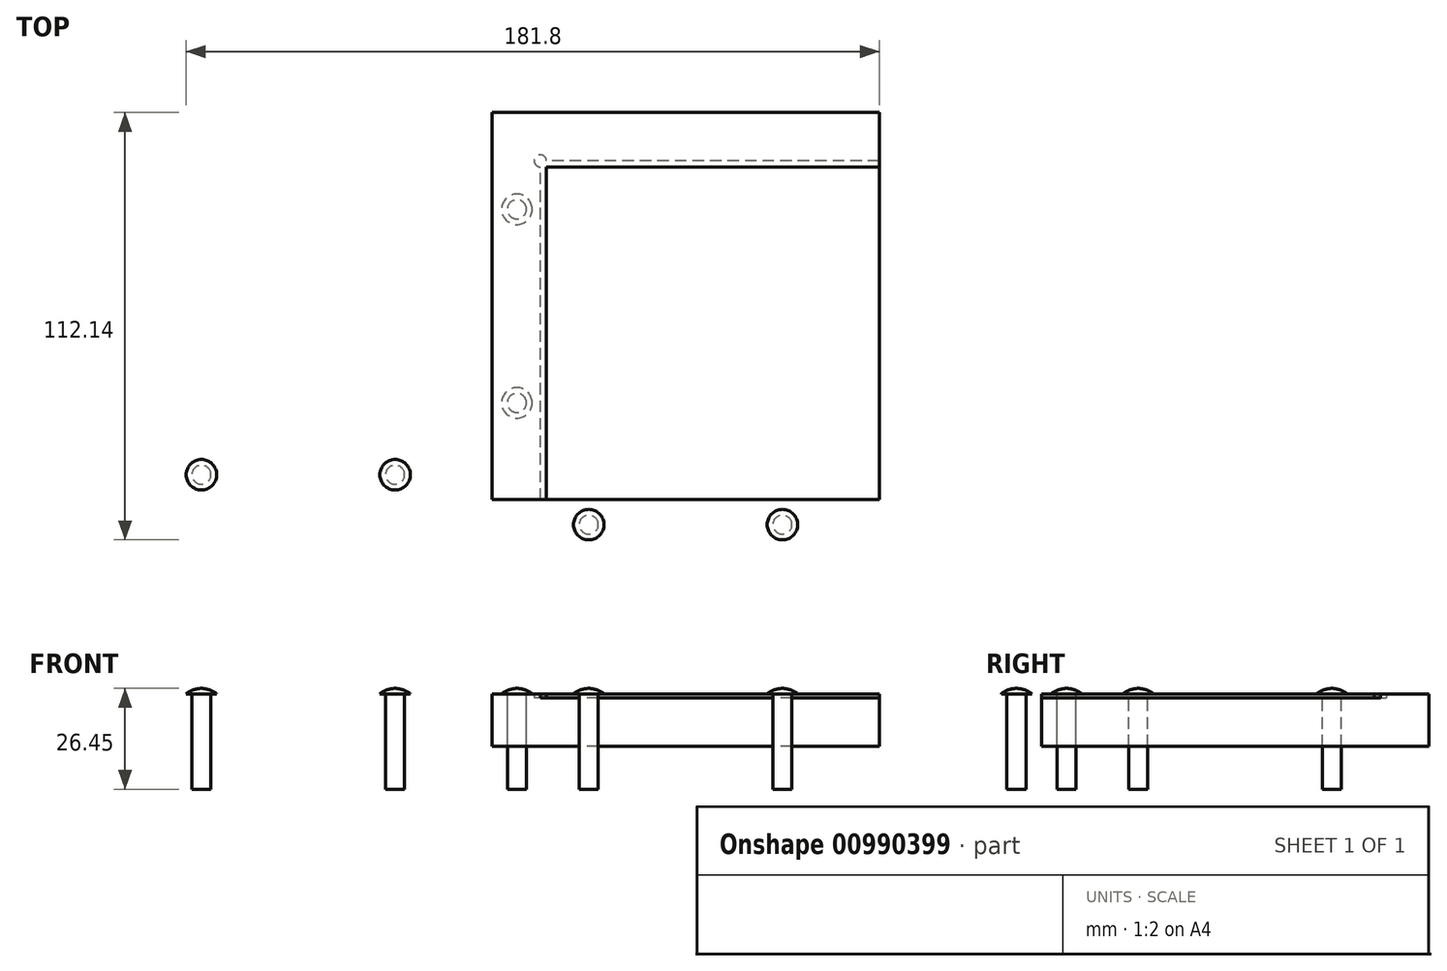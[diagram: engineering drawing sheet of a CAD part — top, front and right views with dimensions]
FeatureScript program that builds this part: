
annotation { "Feature Type Name" : "Feature", "Feature Type Description" : "" }
export const myFeature = defineFeature(function(context is Context, id is Id, definition is map)
    precondition{}
    {
        {
            var Q0;
            Q0=qCreatedBy(makeId("Top.planeOp"),FACE);
            var sketch = newSketch(context, id + "F0", { "sketchPlane" : qUnion([Q0])});
            skLineSegment(sketch, "E0.bottom", {"start": v(50.8, 50.8) * mm, "end": v(-50.8, 50.8) * mm});
            skLineSegment(sketch, "E0.top", {"start": v(50.8, -50.8) * mm, "end": v(-50.8, -50.8) * mm});
            skLineSegment(sketch, "E0.left", {"start": v(50.8, 50.8) * mm, "end": v(50.8, -50.8) * mm});
            skLineSegment(sketch, "E0.right", {"start": v(-50.8, 50.8) * mm, "end": v(-50.8, -50.8) * mm});
            skPoint(sketch, "E0.middle", {"position": v(0, 0) * mm});
            skSolve(sketch);
        }
        {
            var Q0;
            Q0=makeQuery(id+"F0.imprint","IMPRINT",FACE,{"disambiguationData":[TD([[makeQuery(id+"F0.imprint","IMPRINT",EDGE,{"derivedFrom":sQuery(id+"F0.wireOp",EDGE,"E0.bottom")}),1.0]])]});
            extrude(context, id + "F1", {"entities" : qUnion([Q0]), "depth" : 12.7 * mm, "offsetDistance" : 25.4 * mm});
        }
        {
            var Q0;
            Q0=makeQuery(id+"F1.opExtrude","CAP_FACE",FACE,{"disambiguationData":[OSD([sQuery(id+"F0.wireOp",EDGE,"E0.bottom"),sQuery(id+"F0.wireOp",EDGE,"E0.top"),sQuery(id+"F0.wireOp",EDGE,"E0.left"),sQuery(id+"F0.wireOp",EDGE,"E0.right")])],"isStart":false});
            var sketch = newSketch(context, id + "F2", { "sketchPlane" : qUnion([Q0])});
            skLineSegment(sketch, "E1.bottom", {"start": v(50.8, -50.8) * mm, "end": v(-38.1, -50.8) * mm});
            skLineSegment(sketch, "E1.top", {"start": v(50.8, 38.1) * mm, "end": v(-36.51, 38.1) * mm});
            skLineSegment(sketch, "E1.left", {"start": v(50.8, -50.8) * mm, "end": v(50.8, 38.1) * mm});
            skLineSegment(sketch, "E1.right", {"start": v(-38.1, -50.8) * mm, "end": v(-38.1, 36.51) * mm});
            skArc(sketch, "E2", {"start": v(-36.51, 38.1) * mm, "mid": v(-39.22, 39.22) * mm, "end": v(-38.1, 36.51) * mm});
            skLineSegment(sketch, "E3.bottom", {"start": v(-38.1, -50.8) * mm, "end": v(-36.51, -50.8) * mm});
            skLineSegment(sketch, "E3.top", {"start": v(-36.51, 38.1) * mm, "end": v(-36.51, 38.1) * mm});
            skLineSegment(sketch, "E3.right", {"start": v(-36.51, -50.8) * mm, "end": v(-36.51, 36.51) * mm});
            skLineSegment(sketch, "E4.top", {"start": v(50.8, 36.51) * mm, "end": v(-36.51, 36.51) * mm});
            skLineSegment(sketch, "E4.left", {"start": v(50.8, 38.1) * mm, "end": v(50.8, 36.51) * mm});
            skSolve(sketch);
        }
        {
            var Q0;
            Q0=makeQuery(id+"F2.imprint","IMPRINT",FACE,{"disambiguationData":[TD([[makeQuery(id+"F2.imprint","IMPRINT",EDGE,{"derivedFrom":sQuery(id+"F2.wireOp",EDGE,"E2")}),-1.0]])]});
            extrude(context, id + "F3", {"entities" : qUnion([Q0]), "operationType" : NewBodyOperationType.ADD, "depth" : 1 * mm, "offsetDistance" : 25.4 * mm});
        }
        {
            var Q0;
            Q0=makeQuery(id+"F3.opExtrude","CAP_FACE",FACE,{"disambiguationData":[OSD([sQuery(id+"F0.wireOp",EDGE,"E0.bottom"),sQuery(id+"F0.wireOp",EDGE,"E0.top"),sQuery(id+"F0.wireOp",EDGE,"E0.left"),sQuery(id+"F0.wireOp",EDGE,"E0.right"),sQuery(id+"F2.wireOp",EDGE,"E2"),sQuery(id+"F2.wireOp",EDGE,"E3.top"),sQuery(id+"F2.wireOp",EDGE,"E1.right"),sQuery(id+"F2.wireOp",EDGE,"E1.top")])],"isStart":false});
            var sketch = newSketch(context, id + "F4", { "sketchPlane" : qUnion([Q0])});
            skLineSegment(sketch, "E5.0", {"start": v(50.8, 50.8) * mm, "end": v(-50.8, 50.8) * mm});
            skLineSegment(sketch, "E5.1", {"start": v(50.8, -50.8) * mm, "end": v(-50.8, -50.8) * mm});
            skLineSegment(sketch, "E5.2", {"start": v(50.8, 50.8) * mm, "end": v(50.8, -50.8) * mm});
            skLineSegment(sketch, "E5.3", {"start": v(-50.8, 50.8) * mm, "end": v(-50.8, -50.8) * mm});
            skPoint(sketch, "E5.4", {"position": v(0, 0) * mm});
            skLineSegment(sketch, "E5.5", {"start": v(50.8, -50.8) * mm, "end": v(-38.1, -50.8) * mm});
            skLineSegment(sketch, "E5.6", {"start": v(50.8, 38.1) * mm, "end": v(-36.51, 38.1) * mm});
            skLineSegment(sketch, "E5.7", {"start": v(50.8, -50.8) * mm, "end": v(50.8, 38.1) * mm});
            skLineSegment(sketch, "E5.8", {"start": v(-38.1, -50.8) * mm, "end": v(-38.1, 36.51) * mm});
            skArc(sketch, "E5.9", {"start": v(-36.51, 38.1) * mm, "mid": v(-39.22, 39.22) * mm, "end": v(-38.1, 36.51) * mm});
            skLineSegment(sketch, "E5.10", {"start": v(-38.1, -50.8) * mm, "end": v(-36.51, -50.8) * mm});
            skLineSegment(sketch, "E5.11", {"start": v(-36.51, 38.1) * mm, "end": v(-34.93, 38.1) * mm});
            skLineSegment(sketch, "E5.12", {"start": v(-38.1, -50.8) * mm, "end": v(-38.1, 36.51) * mm});
            skLineSegment(sketch, "E5.13", {"start": v(-36.51, -50.8) * mm, "end": v(-36.51, 36.51) * mm});
            skLineSegment(sketch, "E5.14", {"start": v(50.8, 38.1) * mm, "end": v(-36.51, 38.1) * mm});
            skLineSegment(sketch, "E5.15", {"start": v(50.8, 36.51) * mm, "end": v(-36.51, 36.51) * mm});
            skLineSegment(sketch, "E5.16", {"start": v(50.8, 38.1) * mm, "end": v(50.8, 36.51) * mm});
            skPoint(sketch, "E6", {"position": v(-44.26, 25.4) * mm});
            skSolve(sketch);
        }
        {
            var Q0;
            Q0=makeQuery(id+"F4.imprint","IMPRINT",FACE,{"disambiguationData":[TD([[makeQuery(id+"F4.imprint","IMPRINT",EDGE,{"derivedFrom":sQuery(id+"F4.wireOp",EDGE,"E5.0")}),1.0]])]});
            var Q1;
            Q1=makeQuery(id+"F4.imprint","IMPRINT",FACE,{"disambiguationData":[TD([[makeQuery(id+"F4.imprint","IMPRINT",EDGE,{"derivedFrom":sQuery(id+"F4.wireOp",EDGE,"E5.9")}),1.0]])]});
            extrude(context, id + "F5", {"entities" : qUnion([Q0, Q1]), "depth" : 1 / 203.2 * mm, "offsetDistance" : 25.4 * mm});
        }
        {
            var Q0;
            Q0=sQuery(id+"F4.wireOp",VERTEX,"E6");
            var Q1;
            Q1=qCreatedBy(makeId("Front.planeOp"),FACE);
            cPlane(context, id + "F6", {"entities" : qUnion([Q0, Q1]), "cplaneType" : CPlaneType.PLANE_POINT, "offset" : 25.4 * mm, "width" : 152.4 * mm, "height" : 152.4 * mm});
        }
        {
            var Q0;
            Q0=qCreatedBy(id+"F6.planeOp",FACE);
            var sketch = newSketch(context, id + "F7", { "sketchPlane" : qUnion([Q0])});
            skLineSegment(sketch, "E7", {"start": v(-46.76, 13.7) * mm, "end": v(-46.76, -11.3) * mm});
            skLineSegment(sketch, "E8", {"start": v(-46.76, -11.3) * mm, "end": v(-44.26, -11.3) * mm});
            skLineSegment(sketch, "E9", {"start": v(-44.26, -11.3) * mm, "end": v(-44.26, 15.15) * mm});
            skLineSegment(sketch, "E10", {"start": v(-46.76, 13.7) * mm, "end": v(-48.26, 13.7) * mm});
            skArc(sketch, "E11", {"start": v(-44.26, 15.15) * mm, "mid": v(-46.38, 14.78) * mm, "end": v(-48.26, 13.7) * mm});
            skPoint(sketch, "E12.orphan", {"position": v(-40.26, 13.7) * mm});
            skPoint(sketch, "E13", {"position": v(-44.26, 13.7) * mm});
            skLineSegment(sketch, "E14.bottom", {"start": v(-44.26, 13.7) * mm, "end": v(-46.5, 13.7) * mm});
            skLineSegment(sketch, "E14.top", {"start": v(-44.26, -11.3) * mm, "end": v(-46.5, -11.3) * mm});
            skLineSegment(sketch, "E14.left", {"start": v(-44.26, 13.7) * mm, "end": v(-44.26, -11.3) * mm});
            skLineSegment(sketch, "E14.right", {"start": v(-46.5, 13.7) * mm, "end": v(-46.5, -11.3) * mm});
            skSolve(sketch);
        }
        {
            var Q0;
            Q0=makeQuery(id+"F7.imprint","IMPRINT",FACE,{"disambiguationData":[TD([[makeQuery(id+"F7.imprint","IMPRINT",EDGE,{"derivedFrom":sQuery(id+"F7.wireOp",EDGE,"E7")}),1.0]])]});
            var Q1;
            Q1=makeQuery(id+"F7.imprint","IMPRINT",FACE,{"disambiguationData":[TD([[makeQuery(id+"F7.imprint","IMPRINT",EDGE,{"derivedFrom":sQuery(id+"F7.wireOp",EDGE,"E14.bottom")}),1.0]])]});
            var Q2;
            Q2=sQuery(id+"F7.wireOp",EDGE,"E14.left");
            revolve(context, id + "F8", {"surfaceOperationType" : NewSurfaceOperationType.NEW, "entities" : qUnion([Q0, Q1]), "axis" : qUnion([Q2]), "revolveType" : RevolveType.FULL});
        }
        {
            var Q0;
            Q0=makeQuery(id+"F8.opRevolve","SWEPT_BODY",BODY,{"disambiguationData":[OSD([sQuery(id+"F7.wireOp",EDGE,"E7"),sQuery(id+"F7.wireOp",EDGE,"E8"),sQuery(id+"F7.wireOp",EDGE,"E9"),sQuery(id+"F7.wireOp",EDGE,"E10"),sQuery(id+"F7.wireOp",EDGE,"E11"),sQuery(id+"F7.wireOp",EDGE,"E14.top"),sQuery(id+"F7.wireOp",EDGE,"E14.left")])]});
            var Q1;
            Q1=qCreatedBy(makeId("Front.planeOp"),FACE);
            mirror(context, id + "F9", {"entities" : qUnion([Q0]), "mirrorPlane" : qUnion([Q1])});
        }
        {
            var Q0;
            Q0=makeQuery(id+"F8.opRevolve","SWEPT_BODY",BODY,{"disambiguationData":[OSD([sQuery(id+"F7.wireOp",EDGE,"E7"),sQuery(id+"F7.wireOp",EDGE,"E8"),sQuery(id+"F7.wireOp",EDGE,"E9"),sQuery(id+"F7.wireOp",EDGE,"E10"),sQuery(id+"F7.wireOp",EDGE,"E11"),sQuery(id+"F7.wireOp",EDGE,"E14.top"),sQuery(id+"F7.wireOp",EDGE,"E14.left")])]});
            var Q1;
            Q1=makeQuery(id+"F9.opPattern","COPY",BODY,{"derivedFrom":makeQuery(id+"F8.opRevolve","SWEPT_BODY",BODY,{"disambiguationData":[OSD([sQuery(id+"F7.wireOp",EDGE,"E7"),sQuery(id+"F7.wireOp",EDGE,"E8"),sQuery(id+"F7.wireOp",EDGE,"E9"),sQuery(id+"F7.wireOp",EDGE,"E10"),sQuery(id+"F7.wireOp",EDGE,"E11"),sQuery(id+"F7.wireOp",EDGE,"E14.top"),sQuery(id+"F7.wireOp",EDGE,"E14.left")])]}),"instanceName":"1"});
            var Q2;
            {var subQ0=sQuery(id+"F0.wireOp",EDGE,"E0.right");var subQ1=sQuery(id+"F0.wireOp",EDGE,"E0.top");Q2=makeQuery(id+"F3.boolean.opBoolean","MERGE",EDGE,{"derivedFrom":[makeQuery(id+"F1.opExtrude","SWEPT_EDGE",EDGE,{"disambiguationData":[OSD([subQ1,subQ0])]}),makeQuery(id+"F3.opExtrude","SWEPT_EDGE",EDGE,{"disambiguationData":[OSD([subQ1,subQ0])]})]});}
            circularPattern(context, id + "F10", {"entities" : qUnion([Q0, Q1]), "axis" : qUnion([Q2]), "angle" : 90 * degree, "instanceCount" : 2, "equalSpace" : true, "isCentered" : true});
        }
    });
